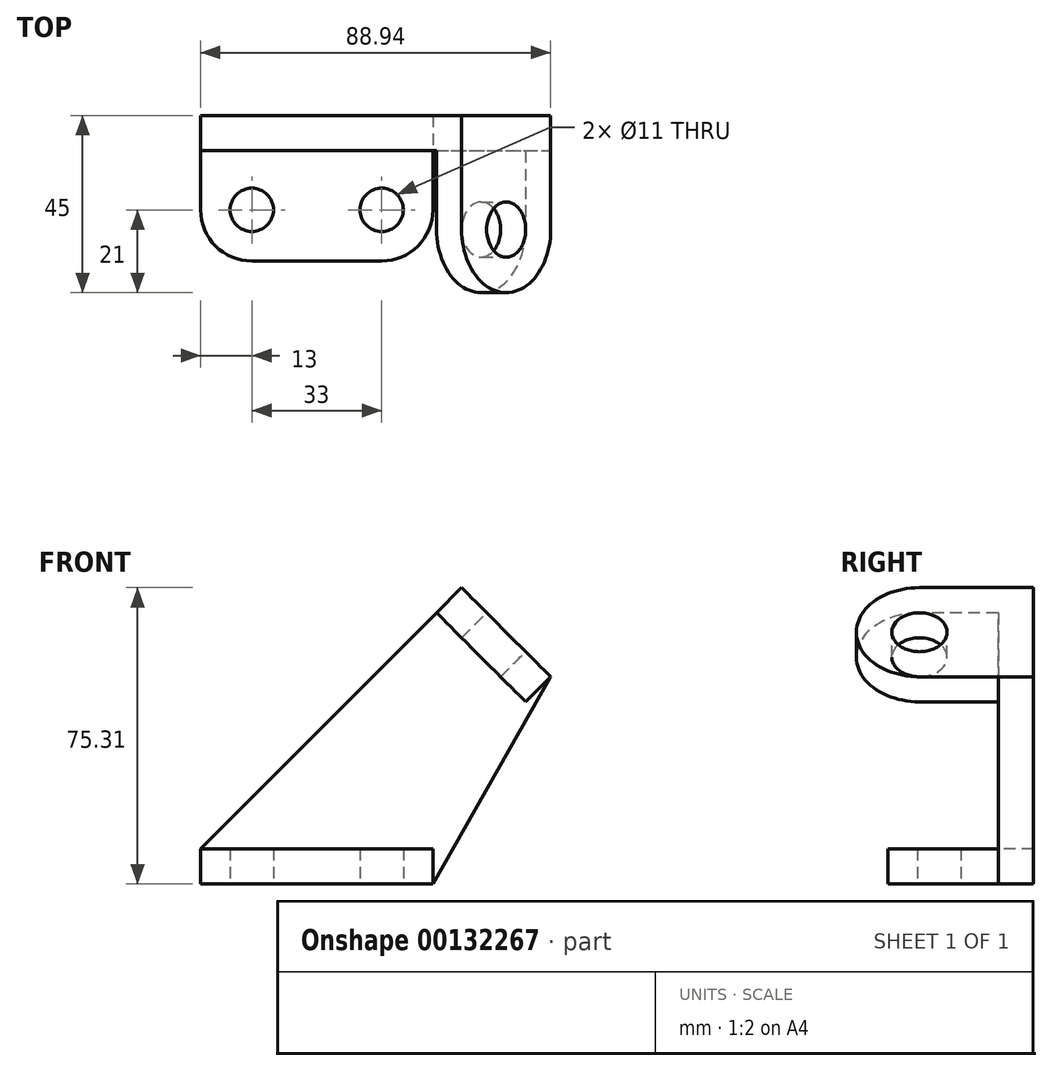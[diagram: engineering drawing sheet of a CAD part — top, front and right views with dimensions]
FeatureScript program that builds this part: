
annotation { "Feature Type Name" : "Feature", "Feature Type Description" : "" }
export const myFeature = defineFeature(function(context is Context, id is Id, definition is map)
    precondition{}
    {
        {
            var Q0;
            Q0=qCreatedBy(makeId("Top.planeOp"),FACE);
            var sketch = newSketch(context, id + "F0", { "sketchPlane" : qUnion([Q0])});
            skLineSegment(sketch, "E0", {"start": v(0, 0) * mm, "end": v(33, 0) * mm});
            skCircle(sketch, "E1", {"center": v(0, -15) * mm, "radius": 5.5 * mm});
            skCircle(sketch, "E2", {"center": v(33, -15) * mm, "radius": 5.5 * mm});
            skArc(sketch, "E3", {"start": v(-13, -15) * mm, "mid": v(-9.2, -24.2) * mm, "end": v(0, -28) * mm});
            skArc(sketch, "E4", {"start": v(33, -28) * mm, "mid": v(42.2, -24.2) * mm, "end": v(46, -15) * mm});
            skLineSegment(sketch, "E5", {"start": v(-13, -15) * mm, "end": v(-13, 0) * mm});
            skLineSegment(sketch, "E6", {"start": v(-13, 0) * mm, "end": v(0, 0) * mm});
            skLineSegment(sketch, "E7", {"start": v(46, -15) * mm, "end": v(46, 0) * mm});
            skLineSegment(sketch, "E8", {"start": v(46, 0) * mm, "end": v(33, 0) * mm});
            skLineSegment(sketch, "E9", {"start": v(33, -28) * mm, "end": v(0, -28) * mm});
            skSolve(sketch);
        }
        {
            var Q0;
            Q0 = qSketchRegion(id + "F0", true);
            extrude(context, id + "F1", {"entities" : qUnion([Q0]), "depth" : 9 * mm});
        }
        {
            var Q0;
            Q0=makeQuery(id+"F1.opExtrude","SWEPT_FACE",FACE,{"disambiguationData":[OSD([sQuery(id+"F0.wireOp",EDGE,"E0"),sQuery(id+"F0.wireOp",EDGE,"E6"),sQuery(id+"F0.wireOp",EDGE,"E8")])]});
            var sketch = newSketch(context, id + "F2", { "sketchPlane" : qUnion([Q0])});
            skLineSegment(sketch, "E10", {"start": v(-46, 0) * mm, "end": v(-75.94, 52.69) * mm});
            skLineSegment(sketch, "E11", {"start": v(13, 9) * mm, "end": v(-53.31, 75.31) * mm});
            skLineSegment(sketch, "E12", {"start": v(-75.94, 52.69) * mm, "end": v(-53.31, 75.31) * mm});
            skLineSegment(sketch, "E13", {"start": v(-46, 0) * mm, "end": v(13, 0) * mm});
            skLineSegment(sketch, "E14", {"start": v(13, 0) * mm, "end": v(13, 9) * mm});
            skLineSegment(sketch, "E15", {"start": v(-64.63, 64) * mm, "end": v(-80.23, 64) * mm, "construction": true});
            skSolve(sketch);
        }
        {
            var Q0;
            Q0 = qSketchRegion(id + "F2", true);
            extrude(context, id + "F3", {"entities" : qUnion([Q0]), "operationType" : NewBodyOperationType.ADD, "depth" : 9 * mm});
        }
        {
            var Q0;
            Q0=makeQuery(id+"F3.opExtrude","SWEPT_FACE",FACE,{"disambiguationData":[OSD([sQuery(id+"F2.wireOp",EDGE,"E12")])]});
            var sketch = newSketch(context, id + "F4", { "sketchPlane" : qUnion([Q0])});
            skLineSegment(sketch, "E16", {"start": v(9, 15.56) * mm, "end": v(-20, 15.56) * mm});
            skPoint(sketch, "E16.endSnap0", {"position": v(4.5, 15.56) * mm});
            skLineSegment(sketch, "E17", {"start": v(9, -16.44) * mm, "end": v(-20, -16.44) * mm});
            skLineSegment(sketch, "E18", {"start": v(9, -16.44) * mm, "end": v(9, 15.56) * mm});
            skCircle(sketch, "E19", {"center": v(-20, -0.44) * mm, "radius": 7 * mm});
            skArc(sketch, "E20", {"start": v(-20, 15.56) * mm, "mid": v(-36, -0.44) * mm, "end": v(-20, -16.44) * mm});
            skSolve(sketch);
        }
        {
            var Q0;
            Q0 = qSketchRegion(id + "F4", true);
            extrude(context, id + "F5", {"entities" : qUnion([Q0]), "operationType" : NewBodyOperationType.ADD, "oppositeDirection" : true, "depth" : 9 * mm});
        }
    });
